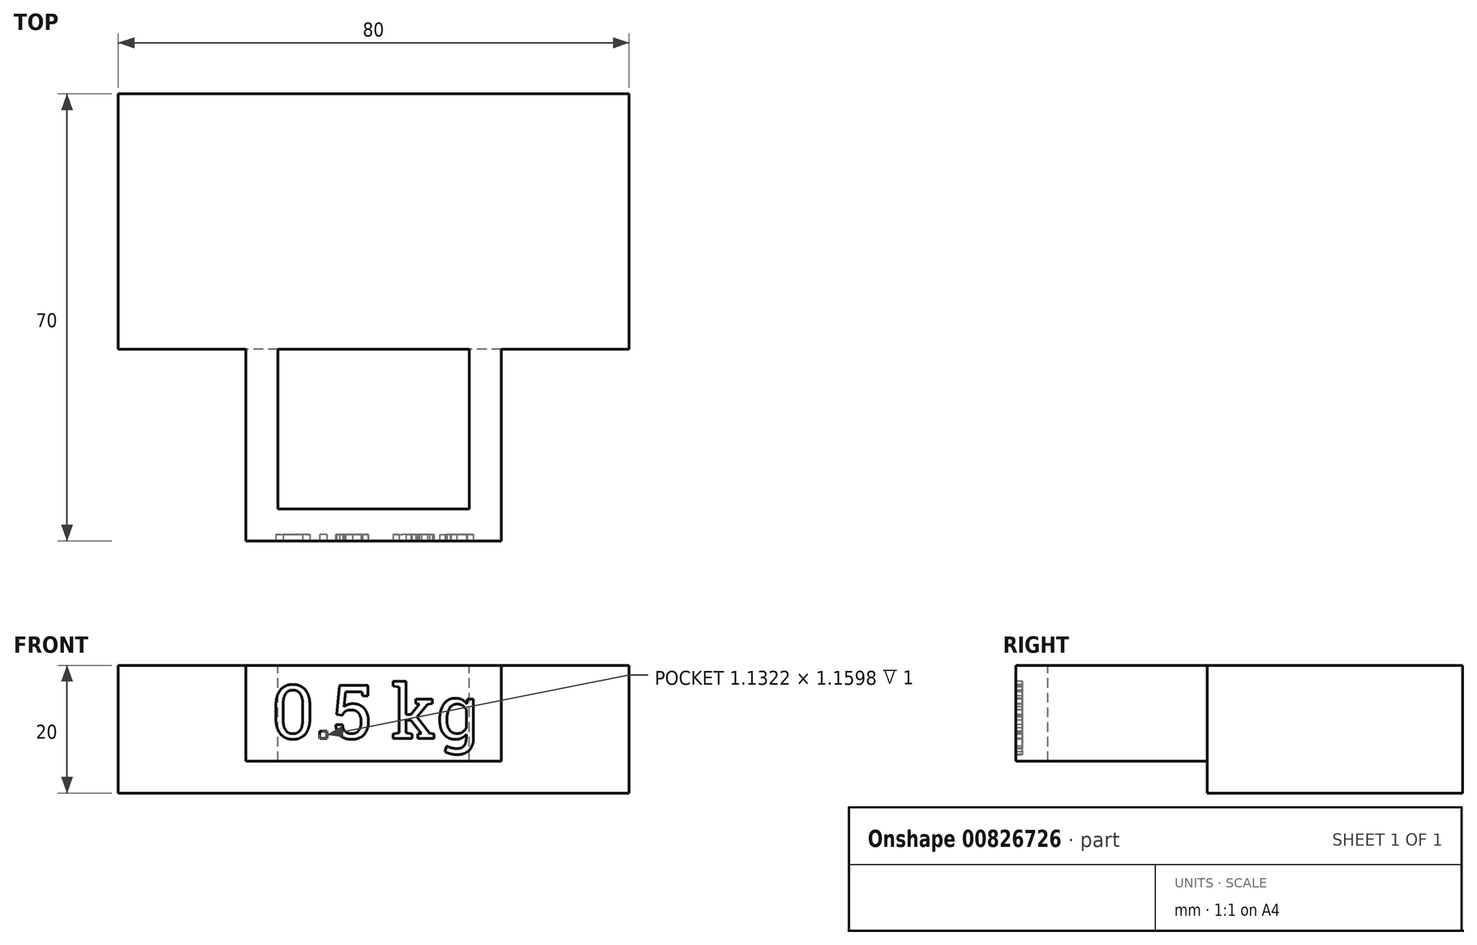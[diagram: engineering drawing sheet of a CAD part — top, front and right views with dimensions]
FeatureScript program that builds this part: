
annotation { "Feature Type Name" : "Feature", "Feature Type Description" : "" }
export const myFeature = defineFeature(function(context is Context, id is Id, definition is map)
    precondition{}
    {
        {
            var Q0;
            Q0=qCreatedBy(makeId("Top.planeOp"),FACE);
            var sketch = newSketch(context, id + "F0", { "sketchPlane" : qUnion([Q0])});
            skLineSegment(sketch, "E0.bottom", {"start": v(40, 20) * mm, "end": v(-40, 20) * mm});
            skLineSegment(sketch, "E0.top", {"start": v(40, -20) * mm, "end": v(-40, -20) * mm});
            skLineSegment(sketch, "E0.left", {"start": v(40, 20) * mm, "end": v(40, -20) * mm});
            skLineSegment(sketch, "E0.right", {"start": v(-40, 20) * mm, "end": v(-40, -20) * mm});
            skPoint(sketch, "E0.middle", {"position": v(0, 0) * mm});
            skSolve(sketch);
        }
        {
            var Q0;
            Q0=makeQuery(id+"F0.imprint","IMPRINT",FACE,{"disambiguationData":[TD([[makeQuery(id+"F0.imprint","IMPRINT",EDGE,{"derivedFrom":sQuery(id+"F0.wireOp",EDGE,"E0.bottom")}),1.0]])]});
            extrude(context, id + "F1", {"entities" : qUnion([Q0]), "depth" : 20 * mm});
        }
        {
            var Q0;
            Q0=makeQuery(id+"F1.opExtrude","CAP_FACE",FACE,{"disambiguationData":[OSD([sQuery(id+"F0.wireOp",EDGE,"E0.bottom"),sQuery(id+"F0.wireOp",EDGE,"E0.top"),sQuery(id+"F0.wireOp",EDGE,"E0.left"),sQuery(id+"F0.wireOp",EDGE,"E0.right")])],"isStart":false});
            var sketch = newSketch(context, id + "F2", { "sketchPlane" : qUnion([Q0])});
            skLineSegment(sketch, "E1.bottom", {"start": v(15, -45) * mm, "end": v(-15, -45) * mm});
            skLineSegment(sketch, "E1.top", {"start": v(15, 5) * mm, "end": v(-15, 5) * mm});
            skLineSegment(sketch, "E1.left", {"start": v(15, -45) * mm, "end": v(15, 5) * mm});
            skLineSegment(sketch, "E1.right", {"start": v(-15, -45) * mm, "end": v(-15, 5) * mm});
            skPoint(sketch, "E1.middle", {"position": v(0, -20) * mm});
            skLineSegment(sketch, "E2.bottom", {"start": v(20, -50) * mm, "end": v(-20, -50) * mm});
            skLineSegment(sketch, "E2.top", {"start": v(20, 10) * mm, "end": v(-20, 10) * mm});
            skLineSegment(sketch, "E2.left", {"start": v(20, -50) * mm, "end": v(20, 10) * mm});
            skLineSegment(sketch, "E2.right", {"start": v(-20, -50) * mm, "end": v(-20, 10) * mm});
            skSolve(sketch);
        }
        {
            var Q0;
            {var subQ7=sQuery(id+"F2.wireOp",EDGE,"E1.bottom");Q0=makeQuery(id+"F2.imprint","IMPRINT",FACE,{"disambiguationData":[TD([[makeQuery(id+"F2.imprint","IMPRINT",EDGE,{"derivedFrom":subQ7}),1.0]])]});}
            extrude(context, id + "F3", {"entities" : qUnion([Q0]), "operationType" : NewBodyOperationType.ADD, "oppositeDirection" : true, "depth" : 15 * mm});
        }
        {
            var Q0;
            Q0=makeQuery(id+"F3.opExtrude","SWEPT_FACE",FACE,{"disambiguationData":[OSD([sQuery(id+"F2.wireOp",EDGE,"E2.bottom")])]});
            var sketch = newSketch(context, id + "F4", { "sketchPlane" : qUnion([Q0])});
            skText(sketch, "E3", { "text": "0.5 kg", "fontName": "RobotoSlab-Regular.ttf"});
            const initialGuessF4  = {"E3": [-0.016, 0.00853, 1, 0, 0.00847]};
            skSetInitialGuess(sketch, initialGuessF4);
            skSolve(sketch);
        }
        {
            var Q0;
            Q0=qSketchRegion(id+"F4",true);
            var Q1;
            Q1=qConstructionFilter(qBodyType(qCreatedBy(id+"F4",EDGE),BodyType.WIRE),ConstructionObject.NO);
            extrude(context, id + "F5", {"entities" : qUnion([Q0]), "operationType" : NewBodyOperationType.REMOVE, "surfaceEntities" : qUnion([Q1]), "oppositeDirection" : true, "depth" : 1 * mm});
        }
    });
